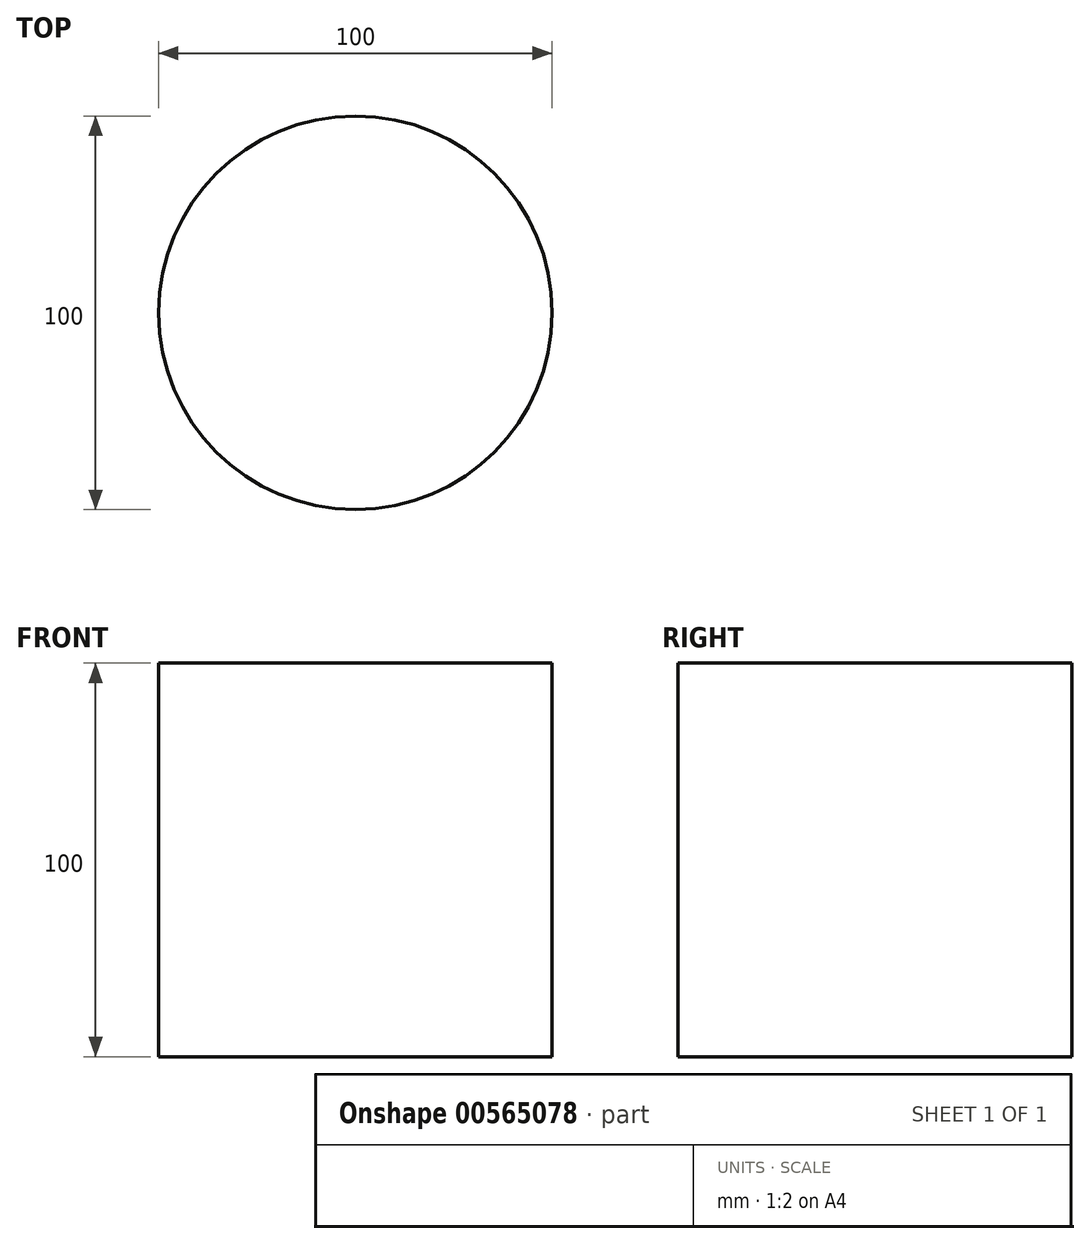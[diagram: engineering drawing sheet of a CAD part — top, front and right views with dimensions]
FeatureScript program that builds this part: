
annotation { "Feature Type Name" : "Feature", "Feature Type Description" : "" }
export const myFeature = defineFeature(function(context is Context, id is Id, definition is map)
    precondition{}
    {
        {
            var Q0;
            Q0=qCreatedBy(makeId("Top.planeOp"),FACE);
            var sketch = newSketch(context, id + "F0", { "sketchPlane" : qUnion([Q0])});
            skCircle(sketch, "E0", {"center": v(0, 0) * mm, "radius": 50 * mm});
            skSolve(sketch);
        }
        {
            var Q0;
            Q0 = qSketchRegion(id + "F0", true);
            extrude(context, id + "F1", {"entities" : qUnion([Q0]), "depth" : 100 * mm, "offsetDistance" : 25 * mm});
        }
    });
